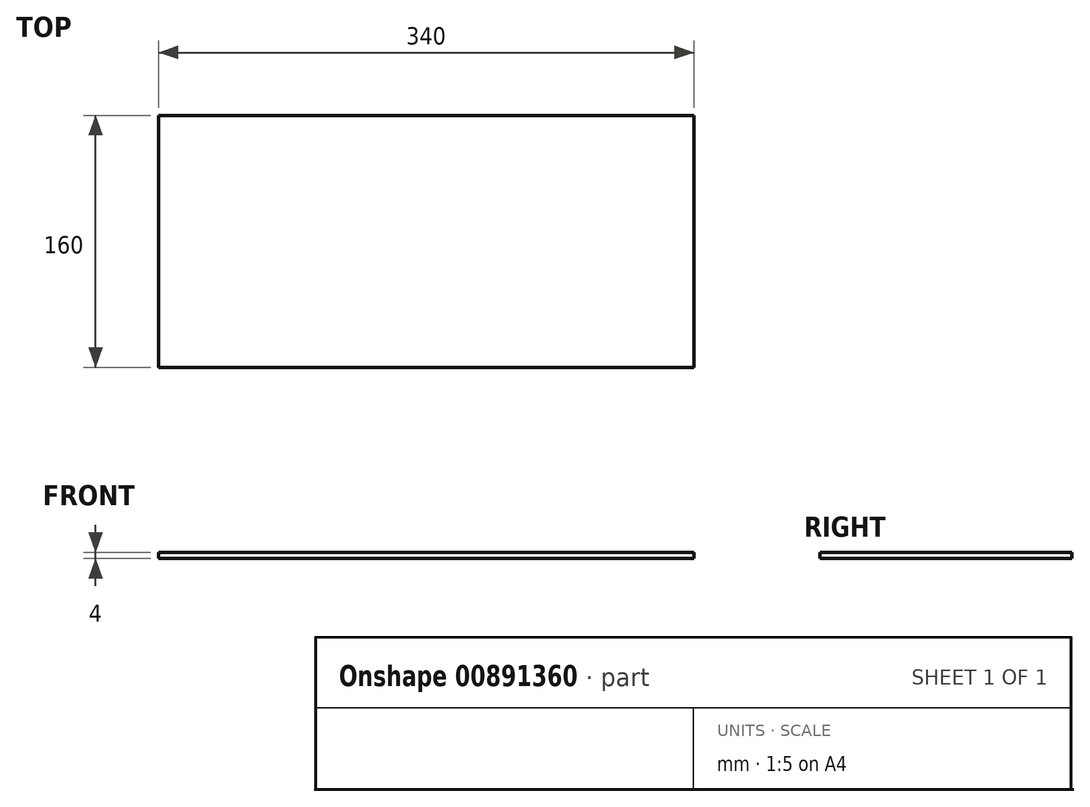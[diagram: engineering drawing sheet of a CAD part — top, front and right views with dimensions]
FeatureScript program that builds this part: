
annotation { "Feature Type Name" : "Feature", "Feature Type Description" : "" }
export const myFeature = defineFeature(function(context is Context, id is Id, definition is map)
    precondition{}
    {
        {
            var Q0;
            Q0=qCreatedBy(makeId("Top.planeOp"),FACE);
            var sketch = newSketch(context, id + "F0", { "sketchPlane" : qUnion([Q0])});
            skLineSegment(sketch, "E0.bottom", {"start": v(170, -80) * mm, "end": v(-170, -80) * mm});
            skLineSegment(sketch, "E0.top", {"start": v(170, 80) * mm, "end": v(-170, 80) * mm});
            skLineSegment(sketch, "E0.left", {"start": v(170, -80) * mm, "end": v(170, 80) * mm});
            skLineSegment(sketch, "E0.right", {"start": v(-170, -80) * mm, "end": v(-170, 80) * mm});
            skPoint(sketch, "E0.middle", {"position": v(0, 0) * mm});
            skSolve(sketch);
        }
        {
            var Q0;
            Q0=makeQuery(id+"F0.imprint","IMPRINT",FACE,{"disambiguationData":[TD([[makeQuery(id+"F0.imprint","IMPRINT",EDGE,{"derivedFrom":sQuery(id+"F0.wireOp",EDGE,"E0.bottom")}),-1.0]])]});
            extrude(context, id + "F1", {"entities" : qUnion([Q0]), "oppositeDirection" : true, "depth" : 4 * mm, "offsetDistance" : 25 * mm});
        }
    });
